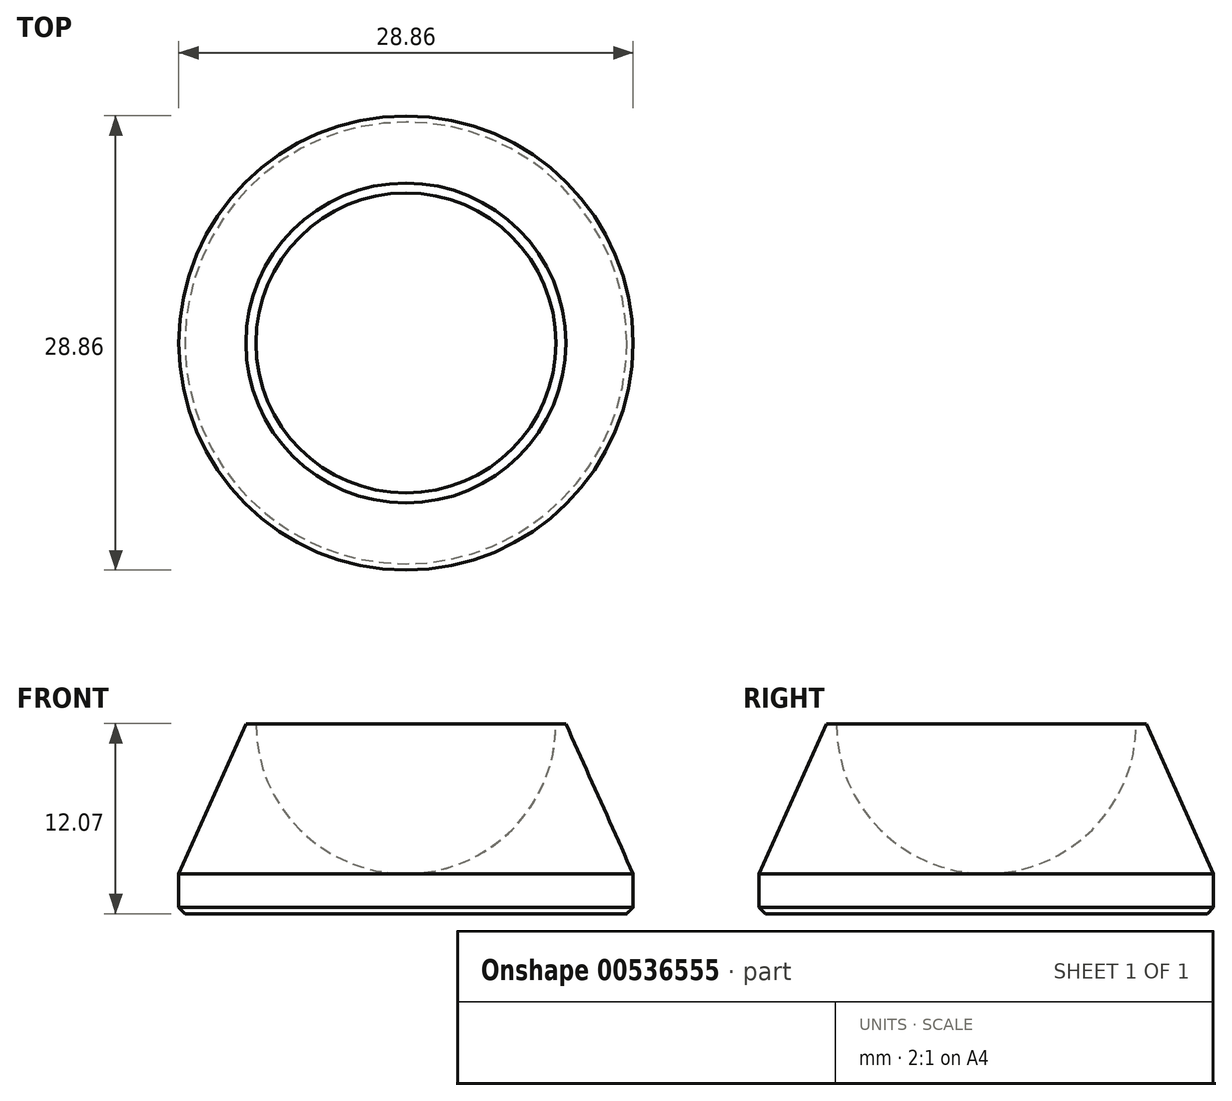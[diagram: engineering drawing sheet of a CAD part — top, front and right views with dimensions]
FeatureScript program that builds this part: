
annotation { "Feature Type Name" : "Feature", "Feature Type Description" : "" }
export const myFeature = defineFeature(function(context is Context, id is Id, definition is map)
    precondition{}
    {
        {
            var Q0;
            Q0=qCreatedBy(makeId("Front.planeOp"),FACE);
            var sketch = newSketch(context, id + "F0", { "sketchPlane" : qUnion([Q0])});
            skLineSegment(sketch, "E0", {"start": v(0, 0) * mm, "end": v(14.43, 0) * mm});
            skLineSegment(sketch, "E1", {"start": v(14.43, 0) * mm, "end": v(14.43, 2.54) * mm});
            skLineSegment(sketch, "E2", {"start": v(14.43, 2.54) * mm, "end": v(10.16, 12.07) * mm, "construction": true});
            skLineSegment(sketch, "E3", {"start": v(10.16, 12.07) * mm, "end": v(9.53, 12.07) * mm});
            skLineSegment(sketch, "E4", {"start": v(0, 0) * mm, "end": v(0, 2.54) * mm});
            skLineSegment(sketch, "E5", {"start": v(9.53, 12.07) * mm, "end": v(0, 12.07) * mm, "construction": true});
            skLineSegment(sketch, "E6", {"start": v(0, 12.07) * mm, "end": v(0, 2.54) * mm, "construction": true});
            skArc(sketch, "E7", {"start": v(0, 2.54) * mm, "mid": v(6.74, 5.33) * mm, "end": v(9.53, 12.07) * mm, "construction": true});
            skLineSegment(sketch, "E8", {"start": v(0, 12.07) * mm, "end": v(10.16, 12.07) * mm, "construction": true});
            skLineSegment(sketch, "E9", {"start": v(10.16, 12.07) * mm, "end": v(14.43, 2.54) * mm});
            skArc(sketch, "E10", {"start": v(0, 2.54) * mm, "mid": v(6.74, 5.33) * mm, "end": v(9.53, 12.07) * mm});
            skSolve(sketch);
        }
        {
            var Q0;
            Q0=qSketchRegion(id+"F0",true);
            var Q1;
            Q1=sQuery(id+"F0.wireOp",EDGE,"E6");
            revolve(context, id + "F1", {"entities" : qUnion([Q0]), "axis" : qUnion([Q1]), "revolveType" : RevolveType.FULL});
        }
        {
            var Q0;
            Q0=makeQuery(id+"F1.opRevolve","SWEPT_EDGE",EDGE,{"disambiguationData":[OSD([sQuery(id+"F0.wireOp",EDGE,"E0"),sQuery(id+"F0.wireOp",EDGE,"E1")])]});
            chamfer(context, id + "F2", {"entities" : qUnion([Q0]), "width" : 0.4 * mm, "tangentPropagation" : true});
        }
    });
